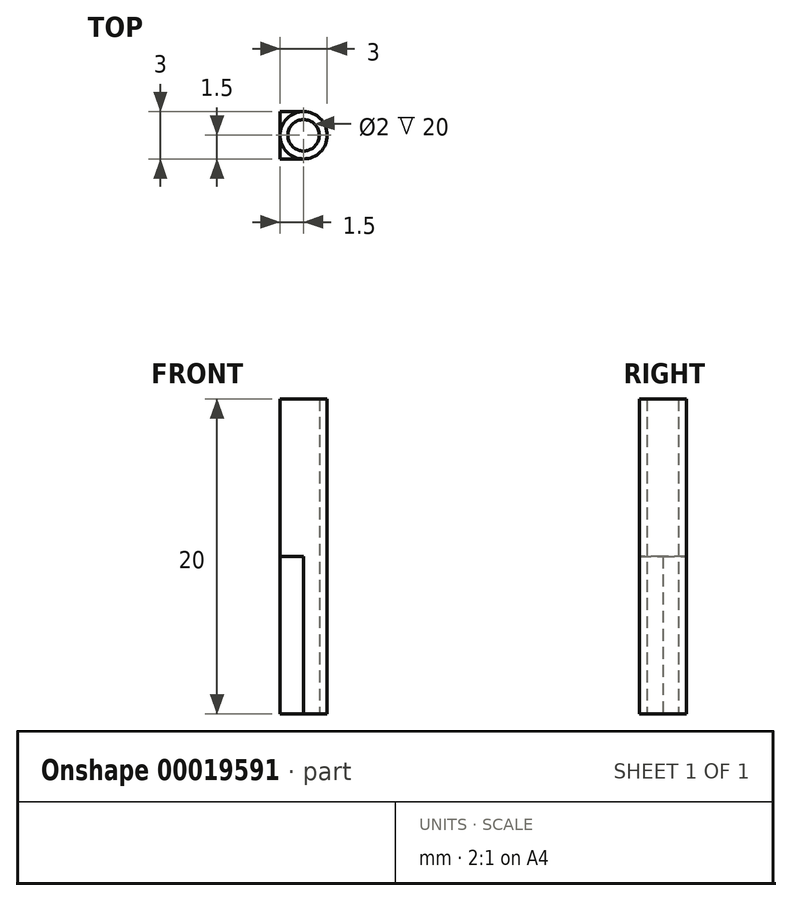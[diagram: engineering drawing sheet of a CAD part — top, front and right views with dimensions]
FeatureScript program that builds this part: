
annotation { "Feature Type Name" : "Feature", "Feature Type Description" : "" }
export const myFeature = defineFeature(function(context is Context, id is Id, definition is map)
    precondition{}
    {
        {
            var Q0;
            Q0=qCreatedBy(makeId("Top.planeOp"),FACE);
            var sketch = newSketch(context, id + "F0", { "sketchPlane" : qUnion([Q0])});
            skCircle(sketch, "E0", {"center": v(0, 0) * mm, "radius": 1.5 * mm});
            skCircle(sketch, "E1.0", {"center": v(0, 0) * mm, "radius": 1 * mm});
            skLineSegment(sketch, "E2", {"start": v(-1.5, 0) * mm, "end": v(-1.5, 1.5) * mm});
            skLineSegment(sketch, "E3", {"start": v(-1.5, 1.5) * mm, "end": v(1.5, 1.5) * mm});
            skLineSegment(sketch, "E4", {"start": v(1.5, 0) * mm, "end": v(1.5, 1.5) * mm});
            skSolve(sketch);
        }
        {
            var Q0;
            Q0=makeQuery(id+"F0.imprint","IMPRINT",FACE,{"disambiguationData":[TD([[makeQuery(id+"F0.imprint","IMPRINT",EDGE,{"derivedFrom":sQuery(id+"F0.wireOp",EDGE,"E0")}),1.0]])]});
            extrude(context, id + "F1", {"entities" : qUnion([Q0]), "depth" : 20 * mm});
        }
        {
            var Q0;
            Q0=makeQuery(id+"F1.opExtrude","CAP_FACE",FACE,{"disambiguationData":[OSD([sQuery(id+"F0.wireOp",EDGE,"E0"),sQuery(id+"F0.wireOp",EDGE,"E1.0")])],"isStart":true});
            var sketch = newSketch(context, id + "F2", { "sketchPlane" : qUnion([Q0])});
            skLineSegment(sketch, "E5", {"start": v(0, 1.5) * mm, "end": v(-1.5, 1.5) * mm});
            skLineSegment(sketch, "E6", {"start": v(-1.5, 1.5) * mm, "end": v(-1.5, -1.5) * mm});
            skLineSegment(sketch, "E7", {"start": v(0, -1.5) * mm, "end": v(-1.5, -1.5) * mm});
            skArc(sketch, "E8", {"start": v(0, 1.5) * mm, "mid": v(-1.5, 0) * mm, "end": v(0, -1.5) * mm});
            skSolve(sketch);
        }
        {
            var Q0;
            {var subQ3=sQuery(id+"F2.wireOp",EDGE,"E5");Q0=makeQuery(id+"F2.imprint","IMPRINT",FACE,{"disambiguationData":[TD([[makeQuery(id+"F2.imprint","IMPRINT",EDGE,{"derivedFrom":subQ3}),1.0]])]});}
            var Q1;
            {var subQ3=sQuery(id+"F2.wireOp",EDGE,"E7");Q1=makeQuery(id+"F2.imprint","IMPRINT",FACE,{"disambiguationData":[TD([[makeQuery(id+"F2.imprint","IMPRINT",EDGE,{"derivedFrom":subQ3}),-1.0]])]});}
            extrude(context, id + "F3", {"entities" : qUnion([Q0, Q1]), "oppositeDirection" : true, "depth" : 10 * mm});
        }
    });
